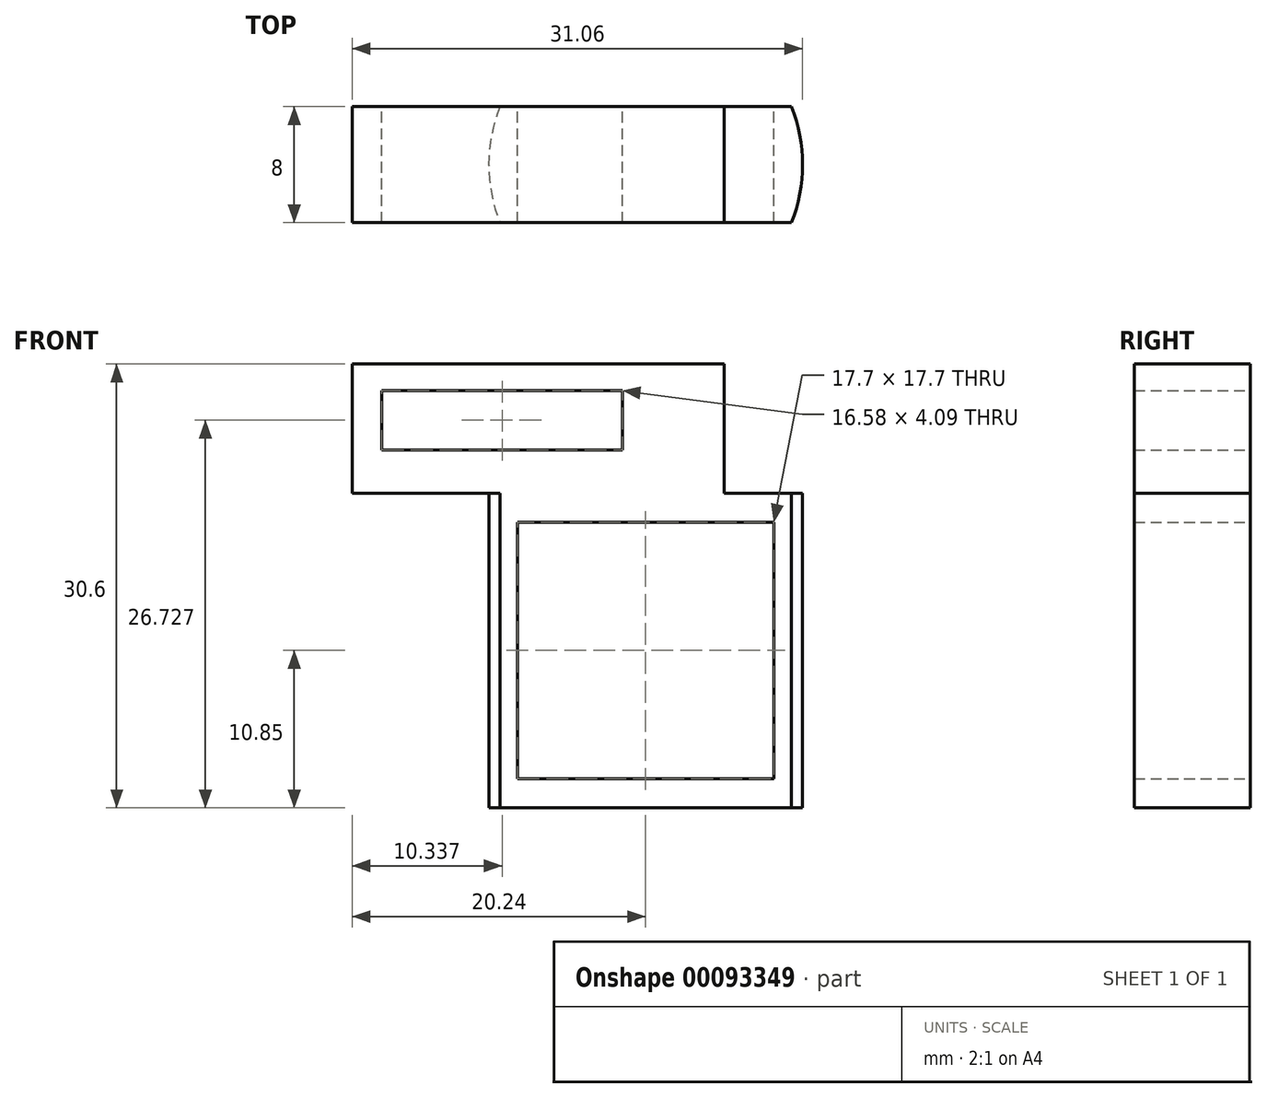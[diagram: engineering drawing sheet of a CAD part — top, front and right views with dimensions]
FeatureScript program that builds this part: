
annotation { "Feature Type Name" : "Feature", "Feature Type Description" : "" }
export const myFeature = defineFeature(function(context is Context, id is Id, definition is map)
    precondition{}
    {
        {
            var Q0;
            Q0=qCreatedBy(makeId("Front.planeOp"),FACE);
            var sketch = newSketch(context, id + "F0", { "sketchPlane" : qUnion([Q0])});
            skCircle(sketch, "E0", {"center": v(0, 0) * mm, "radius": 8.85 * mm});
            skLineSegment(sketch, "E1", {"start": v(0, 8.85) * mm, "end": v(8.85, 0) * mm});
            skLineSegment(sketch, "E2", {"start": v(8.85, 0) * mm, "end": v(8.85, 8.85) * mm});
            skLineSegment(sketch, "E3", {"start": v(8.85, 8.85) * mm, "end": v(0, 8.85) * mm});
            skLineSegment(sketch, "E4.MirrorCS", {"start": v(8.85, -8.85) * mm, "end": v(0, -8.85) * mm});
            skLineSegment(sketch, "E5.MirrorCS", {"start": v(8.85, 0) * mm, "end": v(8.85, -8.85) * mm});
            skLineSegment(sketch, "E6.MirrorCS", {"start": v(-8.85, 8.85) * mm, "end": v(0, 8.85) * mm});
            skLineSegment(sketch, "E7.MirrorCS", {"start": v(-8.85, 0) * mm, "end": v(-8.85, 8.85) * mm});
            skLineSegment(sketch, "E8.MirrorCS", {"start": v(-8.85, -8.85) * mm, "end": v(0, -8.85) * mm});
            skLineSegment(sketch, "E9.MirrorCS", {"start": v(-8.85, 0) * mm, "end": v(-8.85, -8.85) * mm});
            skLineSegment(sketch, "E10.0", {"start": v(-10.85, 0) * mm, "end": v(-10.85, 10.85) * mm});
            skLineSegment(sketch, "E10.1", {"start": v(-10.85, 0) * mm, "end": v(-10.85, -10.85) * mm});
            skLineSegment(sketch, "E10.2", {"start": v(-10.85, 10.85) * mm, "end": v(0, 10.85) * mm});
            skLineSegment(sketch, "E10.3", {"start": v(-10.85, -10.85) * mm, "end": v(0, -10.85) * mm});
            skLineSegment(sketch, "E10.4", {"start": v(10.85, 10.85) * mm, "end": v(0, 10.85) * mm});
            skLineSegment(sketch, "E10.5", {"start": v(10.85, 0) * mm, "end": v(10.85, 10.85) * mm});
            skLineSegment(sketch, "E10.6", {"start": v(10.85, 0) * mm, "end": v(10.85, -10.85) * mm});
            skLineSegment(sketch, "E10.7", {"start": v(10.85, -10.85) * mm, "end": v(0, -10.85) * mm});
            skLineSegment(sketch, "E11.bottom", {"start": v(5.42, 10.85) * mm, "end": v(-20.24, 10.85) * mm});
            skLineSegment(sketch, "E11.top", {"start": v(5.42, 19.75) * mm, "end": v(-20.24, 19.75) * mm});
            skLineSegment(sketch, "E11.left", {"start": v(5.42, 10.85) * mm, "end": v(5.42, 19.75) * mm});
            skLineSegment(sketch, "E11.right", {"start": v(-20.24, 10.85) * mm, "end": v(-20.24, 19.75) * mm});
            skLineSegment(sketch, "E12.bottom", {"start": v(-18.2, 17.92) * mm, "end": v(-1.61, 17.92) * mm});
            skLineSegment(sketch, "E12.top", {"start": v(-18.2, 13.83) * mm, "end": v(-1.61, 13.83) * mm});
            skLineSegment(sketch, "E12.left", {"start": v(-18.2, 17.92) * mm, "end": v(-18.2, 13.83) * mm});
            skLineSegment(sketch, "E12.right", {"start": v(-1.61, 17.92) * mm, "end": v(-1.61, 13.83) * mm});
            skSolve(sketch);
        }
        {
            var Q0;
            Q0=makeQuery(id+"F0.imprint","IMPRINT",FACE,{"disambiguationData":[TD([[makeQuery(id+"F0.imprint","IMPRINT",EDGE,{"derivedFrom":sQuery(id+"F0.wireOp",EDGE,"E2")}),-1.0]])]});
            var Q1;
            Q1=makeQuery(id+"F0.imprint","IMPRINT",FACE,{"disambiguationData":[TD([[makeQuery(id+"F0.imprint","IMPRINT",EDGE,{"derivedFrom":sQuery(id+"F0.wireOp",EDGE,"E11.top")}),1.0]])]});
            extrude(context, id + "F1", {"entities" : qUnion([Q0, Q1]), "depth" : 4 * mm, "hasSecondDirection" : true, "secondDirectionOppositeDirection" : true, "secondDirectionDepth" : 4 * mm});
        }
        {
            var Q0;
            Q0=makeQuery(id+"F1.opExtrude","SWEPT_FACE",FACE,{"disambiguationData":[OSD([sQuery(id+"F0.wireOp",EDGE,"E10.3"),sQuery(id+"F0.wireOp",EDGE,"E10.7")])]});
            var sketch = newSketch(context, id + "F2", { "sketchPlane" : qUnion([Q0])});
            skCircle(sketch, "E13", {"center": v(0, 0) * mm, "radius": 10.82 * mm});
            skLineSegment(sketch, "E14", {"start": v(9.7, 4.81) * mm, "end": v(13.92, 4.81) * mm});
            skLineSegment(sketch, "E15", {"start": v(13.92, 4.81) * mm, "end": v(13.92, -5.04) * mm});
            skLineSegment(sketch, "E16", {"start": v(13.92, -5.04) * mm, "end": v(9.58, -5.04) * mm});
            skLineSegment(sketch, "E17.MirrorCS", {"start": v(-9.7, 4.81) * mm, "end": v(-13.92, 4.81) * mm});
            skLineSegment(sketch, "E18.MirrorCS", {"start": v(-13.92, 4.81) * mm, "end": v(-13.92, -5.04) * mm});
            skLineSegment(sketch, "E19.MirrorCS", {"start": v(-13.92, -5.04) * mm, "end": v(-9.58, -5.04) * mm});
            skSolve(sketch);
        }
        {
            var Q0;
            {var subQ1=sQuery(id+"F0.wireOp",EDGE,"E10.7");var subQ7=makeQuery(id+"F1.opExtrude","SWEPT_EDGE",EDGE,{"disambiguationData":[OSD([sQuery(id+"F0.wireOp",EDGE,"E10.6"),subQ1])]});Q0=makeQuery(id+"F2.imprint","IMPRINT",FACE,{"disambiguationData":[TD([[makeQuery(id+"F2.imprint","IMPRINT",EDGE,{"derivedFrom":subQ7}),-1.0]])]});}
            var Q1;
            {var subQ2=sQuery(id+"F0.wireOp",EDGE,"E10.3");var subQ7=makeQuery(id+"F1.opExtrude","SWEPT_EDGE",EDGE,{"disambiguationData":[OSD([sQuery(id+"F0.wireOp",EDGE,"E10.1"),subQ2])]});Q1=makeQuery(id+"F2.imprint","IMPRINT",FACE,{"disambiguationData":[TD([[makeQuery(id+"F2.imprint","IMPRINT",EDGE,{"derivedFrom":subQ7}),1.0]])]});}
            var Q2;
            {var subQ0=sQuery(id+"FNrOsNvtq1K3209_1.wireOp",EDGE,"wVdfrTCn-lzeS-aEVG-hB8Q-wytQOjNaBdEq");var subQ1=sQuery(id+"FNrOsNvtq1K3209_1.wireOp",EDGE,"J5oflCiJ-X8fM-vOw1-0u6g-H746FkmQtHey");Q2=makeQuery(id+"FSOaAdCP6IGlj0H_1.boolean.opBoolean","SPLIT",FACE,{"disambiguationData":[TD([makeQuery(id+"F1.opExtrude","SWEPT_FACE",FACE,{"disambiguationData":[OSD([sQuery(id+"F0.wireOp",EDGE,"E10.0"),sQuery(id+"F0.wireOp",EDGE,"E10.1")])]})])],"derivedFrom":makeQuery(id+"FSOaAdCP6IGlj0H_1.opExtrude","CAP_FACE",FACE,{"disambiguationData":[OSD([sQuery(id+"FNrOsNvtq1K3209_1.wireOp",EDGE,"q0RaqSpJ-WFI5-aHn9-txQ2-Z0p5vzVhh80B"),sQuery(id+"FNrOsNvtq1K3209_1.wireOp",EDGE,"Nxq4UVsN-DhaE-Qh5w-kfEj-NINk5GcIaqNu"),subQ0,subQ1])],"isStart":true})});}
            extrude(context, id + "F3", {"entities" : qUnion([Q0, Q1]), "operationType" : NewBodyOperationType.REMOVE, "oppositeDirection" : true, "endBoundEntityFace" : qUnion([Q2]), "depth" : 21.7 * mm});
        }
    });
